# Revit family: RN 81049 Optipress-Aquaplus-Flanschübergang PN 16
name_source: partatom
category: Rohrformteile
units: mm (PartAtom-declared; Revit-internal decimal feet)

## family parameters
Arbeitsebenenbasiert = Nein
Beim Laden mit Abzugskörper schneiden = Nein
Bemaßung runder Anschluss = Durchmesser verwenden
Gemeinsam genutzt = Nein
Immer vertikal = Ja
Teiletyp = Verbindung

## types (2) — shared parameters
1.010.00.2 Blattnummer der Richtlinie = 29
1.010.00.3 Ausgabedatum (Monat) der Richtlinie = 201308
1.010.00.4 Herstellername = R. Nussbaum AG
1.010.00.5 Revisionsdatum der Datei = 20190521
1.010.00.6 Webadresse des Herstellers = http://www.nussbaum.ch
1.100.00.4 Produktbezeichnung = Versorgung
1.110.00.2 Index = 4
1.110.00.4 Produktbezeichnung = Optipress
1.960/3L.00.8 Link (URL) = https://www.nussbaum.ch
29.700.00.4 Produktname = Optipress-Aquaplus-Flanschübergang PN 16, mit losem Flansch
29.700.00.5 Produktkennung = 2
29.700.00.6 Querschnittsform = 1
29.700.00.7 Nennweitensystem = DN
29.700.00.8 Nenndrucksystem = PN
29.710.02.4 Nenndruck = 16
29.710.02.5 max. zul. Überdruck [hPa] = 1600
29.710.02.7 max. zul. Dauer-Betriebsdruck [hPa] = 1600
29.710.02.9 max. zul. Dauer-Betriebstemperatur [°C] = 95
CONNECTOR0_dX_00 = 1 mm  [stored 0.00328084 ft]
CONNECTOR0_ref_dX = 1 mm  [stored 0.00328084 ft]
Connector Visibility = Nein
EnclosingSpace Visibility = Nein

## per-type parameters (varying)
| type | 1.800.00.3 TGA-Nummer | 1.810.00.3 Hersteller-Bestellnummer | 1.810.00.4 DATANORM-Nummer | 1.810.00.5 StLB-Nummer | 1.810.00.6 GTIN-Nummer | 29.710.02.10 Formstück-Gewicht [kg] | 29.710.02.3 Benennung | CONNECTOR0_DIAMETER_dX_0r | CONNECTOR1_DIAMETER_dX_0r | CONNECTOR1_dX_00 | CONNECTOR1_dX_01 | CONNECTOR1_ref_dX | R. Nussbaum AG 81049.27 de Visibility | R. Nussbaum AG 81049.28 de Visibility |
| 81049.27, Optipress-Aquaplus-Flanschübergang PN 16, mit losem Flansch, DN=40 | 01900400000000000000000000000000000000000000000043000000000000000001 | 81049.27 | 81049.27 | 267.177 | 7612945022493 | 2.396 | Optipress-Aquaplus-Flanschübergang PN 16, mit losem Flansch, DN=40 | 40 mm  [stored 0.131234 ft] | 40 mm  [stored 0.131234 ft] | 47 mm | 83 mm | 47 mm | Ja | Nein |
| 81049.28, Optipress-Aquaplus-Flanschübergang PN 16, mit losem Flansch, DN=50 | 01900400000000000000000000000000000000000000000043000000000000000002 | 81049.28 | 81049.28 | 267.178 | 7612945022509 | 2.98 | Optipress-Aquaplus-Flanschübergang PN 16, mit losem Flansch, DN=50 | 50 mm | 50 mm | 50 mm | 90 mm | 50 mm | Nein | Ja |

note: column(s) folded — value = type name in every type: 1.800.00.4 Kommentarfeld

note: [stored X ft] marks values corroborated as IEEE doubles in the binary element streams (Revit-internal decimal feet)

## geometry (parser evidence)
native form markers: Sweep x2
no freeform markers — native parametric forms only
